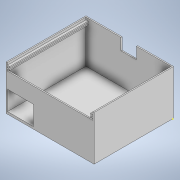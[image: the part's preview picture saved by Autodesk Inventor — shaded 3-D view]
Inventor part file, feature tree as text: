
AUTODESK INVENTOR PART (.ipt)
format: ipt  version: 2022 (Build 260153000, 153)  size: 180,224 bytes
history: native  units: mm
features: sketch x8, extrude x7
ambient origin geometry x8: Origin, YZ Plane, XZ Plane, XY Plane, X Axis, Y Axis, Z Axis, Center Point
bodies: Solid1 (feature_tree)
feature tree (15):
  extrude  "Extrusion1"  Depth=103.0mm
  extrude  "Extrusion2"  Depth=55.0mm TaperAngle=0.0deg
  sketch  "Sketch3"  dims[d11=20.0mm d12=55.0mm d13=0.0mm]
  extrude  "Extrusion3"  Depth=55.0mm TaperAngle=0.0deg
  extrude  "Extrusion4"  Depth=1.5mm
  extrude  "Extrusion5"  Depth=3.0mm TaperAngle=0.0deg
  extrude  "Extrusion6"  Depth=1.5mm
  extrude  "Extrusion7"  Depth=3.0mm TaperAngle=0.0deg
  sketch  "Sketch1"  dims[d0=113.5mm d1=103.0mm]
  sketch  "Sketch2"  dims[d2=3.0mm d3=0.0mm d7=55.0mm d8=0.0mm]
  sketch  "Sketch4"  dims[d14=1.5mm d15=1.5mm]
  sketch  "Sketch5"  dims[d16=1.5mm d17=3.0mm d18=0.0mm]
  sketch  "Sketch6"  dims[d20=1.5mm d21=1.5mm]
  sketch  "Sketch8"  dims[d22=1.5mm d23=3.0mm d24=0.0mm]
  sketch  "Sketch10"  dims[d27=1.5mm d28=1.5mm d29=20.385mm d30=0.0mm d31=0.0mm d33=10.0mm d34=0.0mm d19=0.5mm]
